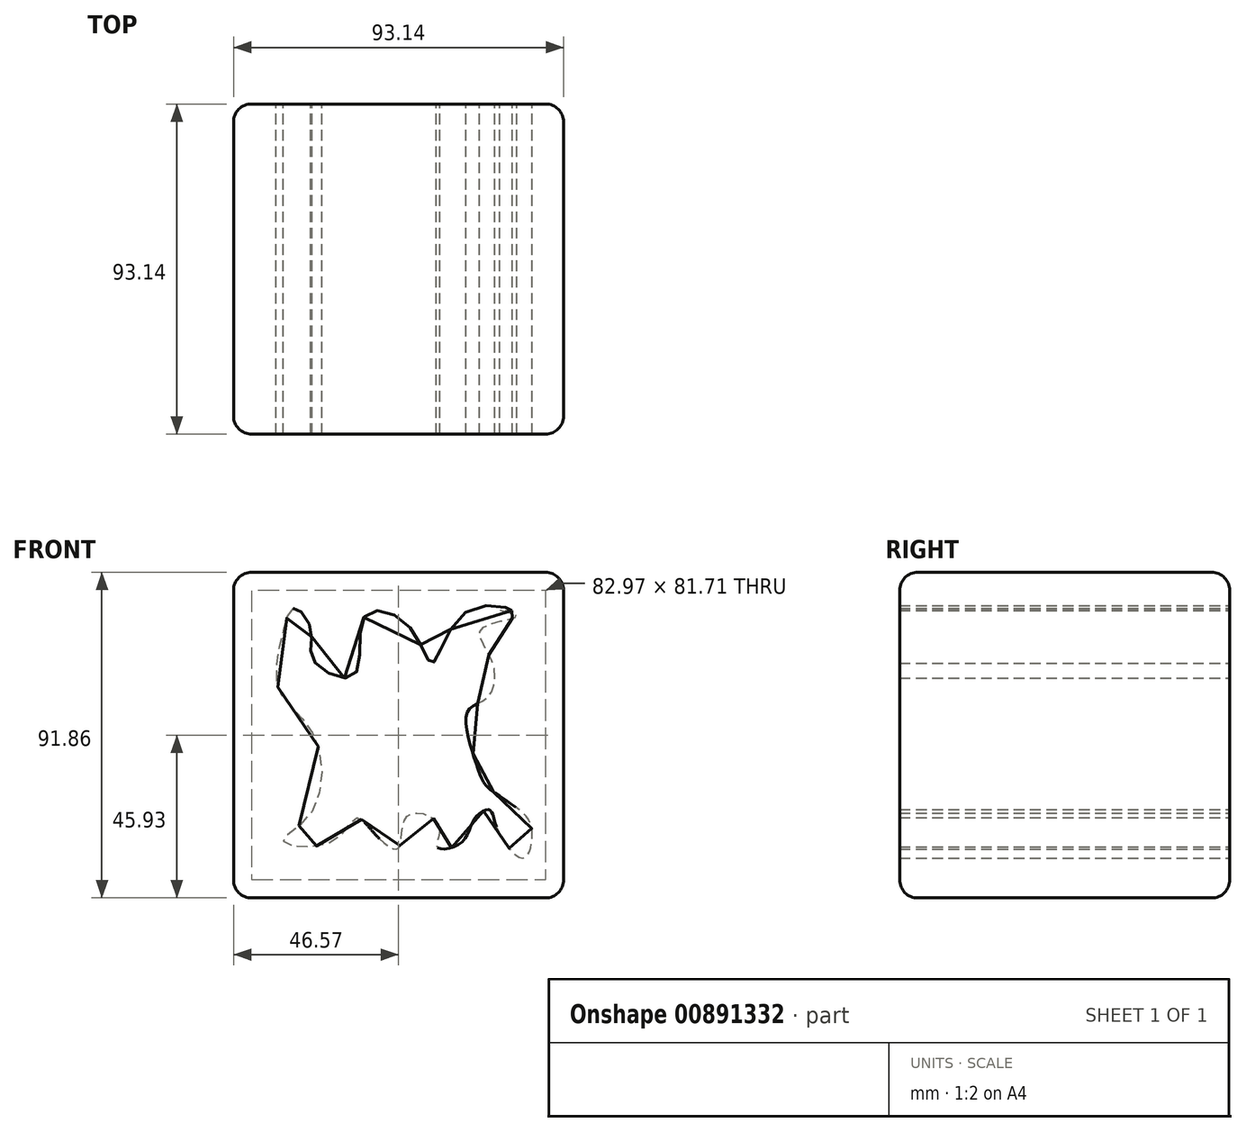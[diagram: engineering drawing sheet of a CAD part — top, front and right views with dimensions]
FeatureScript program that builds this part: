
annotation { "Feature Type Name" : "Feature", "Feature Type Description" : "" }
export const myFeature = defineFeature(function(context is Context, id is Id, definition is map)
    precondition{}
    {
        {
            var Q0;
            Q0=qCreatedBy(makeId("Front.planeOp"),FACE);
            var sketch = newSketch(context, id + "F0", { "sketchPlane" : qUnion([Q0])});
            skLineSegment(sketch, "E0.bottom", {"start": v(46.57, 45.93) * mm, "end": v(-46.57, 45.93) * mm});
            skLineSegment(sketch, "E0.top", {"start": v(46.57, -45.93) * mm, "end": v(-46.57, -45.93) * mm});
            skLineSegment(sketch, "E0.left", {"start": v(46.57, 45.93) * mm, "end": v(46.57, -45.93) * mm});
            skLineSegment(sketch, "E0.right", {"start": v(-46.57, 45.93) * mm, "end": v(-46.57, -45.93) * mm});
            skPoint(sketch, "E0.middle", {"position": v(0, 0) * mm});
            skSolve(sketch);
        }
        {
            var Q0;
            Q0=makeQuery(id+"F0.imprint","IMPRINT",FACE,{"disambiguationData":[TD([[makeQuery(id+"F0.imprint","IMPRINT",EDGE,{"derivedFrom":sQuery(id+"F0.wireOp",EDGE,"E0.bottom")}),1.0]])]});
            extrude(context, id + "F1", {"entities" : qUnion([Q0]), "depth" : 93.14 * mm, "offsetDistance" : 25.4 * mm});
        }
        {
            var Q0;
            Q0=makeQuery(id+"F1.opExtrude","CAP_EDGE",EDGE,{"disambiguationData":[OSD([sQuery(id+"F0.wireOp",EDGE,"E0.bottom")])],"isStart":false});
            var Q1;
            Q1=makeQuery(id+"F1.opExtrude","CAP_EDGE",EDGE,{"disambiguationData":[OSD([sQuery(id+"F0.wireOp",EDGE,"E0.right")])],"isStart":false});
            var Q2;
            Q2=makeQuery(id+"F1.opExtrude","CAP_EDGE",EDGE,{"disambiguationData":[OSD([sQuery(id+"F0.wireOp",EDGE,"E0.top")])],"isStart":false});
            var Q3;
            Q3=makeQuery(id+"F1.opExtrude","CAP_EDGE",EDGE,{"disambiguationData":[OSD([sQuery(id+"F0.wireOp",EDGE,"E0.left")])],"isStart":false});
            var Q4;
            Q4=makeQuery(id+"F1.opExtrude","CAP_EDGE",EDGE,{"disambiguationData":[OSD([sQuery(id+"F0.wireOp",EDGE,"E0.right")])],"isStart":true});
            var Q5;
            Q5=makeQuery(id+"F1.opExtrude","CAP_EDGE",EDGE,{"disambiguationData":[OSD([sQuery(id+"F0.wireOp",EDGE,"E0.bottom")])],"isStart":true});
            var Q6;
            Q6=makeQuery(id+"F1.opExtrude","CAP_FACE",FACE,{"disambiguationData":[OSD([sQuery(id+"F0.wireOp",EDGE,"E0.bottom"),sQuery(id+"F0.wireOp",EDGE,"E0.top"),sQuery(id+"F0.wireOp",EDGE,"E0.left"),sQuery(id+"F0.wireOp",EDGE,"E0.right")])],"isStart":true});
            var Q7;
            Q7=makeQuery(id+"F1.opExtrude","CAP_EDGE",EDGE,{"disambiguationData":[OSD([sQuery(id+"F0.wireOp",EDGE,"E0.top")])],"isStart":true});
            var Q8;
            Q8=makeQuery(id+"F1.opExtrude","CAP_EDGE",EDGE,{"disambiguationData":[OSD([sQuery(id+"F0.wireOp",EDGE,"E0.left")])],"isStart":true});
            var Q9;
            Q9=makeQuery(id+"F1.opExtrude","SWEPT_EDGE",EDGE,{"disambiguationData":[OSD([sQuery(id+"F0.wireOp",EDGE,"E0.bottom"),sQuery(id+"F0.wireOp",EDGE,"E0.left")])]});
            var Q10;
            Q10=makeQuery(id+"F1.opExtrude","SWEPT_EDGE",EDGE,{"disambiguationData":[OSD([sQuery(id+"F0.wireOp",EDGE,"E0.bottom"),sQuery(id+"F0.wireOp",EDGE,"E0.right")])]});
            var Q11;
            Q11=makeQuery(id+"F1.opExtrude","SWEPT_FACE",FACE,{"disambiguationData":[OSD([sQuery(id+"F0.wireOp",EDGE,"E0.left")])]});
            var Q12;
            Q12=makeQuery(id+"F1.opExtrude","SWEPT_EDGE",EDGE,{"disambiguationData":[OSD([sQuery(id+"F0.wireOp",EDGE,"E0.top"),sQuery(id+"F0.wireOp",EDGE,"E0.left")])]});
            var Q13;
            Q13=makeQuery(id+"F1.opExtrude","SWEPT_EDGE",EDGE,{"disambiguationData":[OSD([sQuery(id+"F0.wireOp",EDGE,"E0.top"),sQuery(id+"F0.wireOp",EDGE,"E0.right")])]});
            fillet(context, id + "F2", {"entities" : qUnion([Q0, Q1, Q2, Q3, Q4, Q5, Q6, Q7, Q8, Q9, Q10, Q11, Q12, Q13]), "radius" : 5.08 * mm, "tangentPropagation" : true, "allowEdgeOverflow" : false});
        }
        {
            var Q0;
            Q0=makeQuery(id+"F1.opExtrude","CAP_FACE",FACE,{"disambiguationData":[OSD([sQuery(id+"F0.wireOp",EDGE,"E0.bottom"),sQuery(id+"F0.wireOp",EDGE,"E0.top"),sQuery(id+"F0.wireOp",EDGE,"E0.left"),sQuery(id+"F0.wireOp",EDGE,"E0.right")])],"isStart":false});
            var sketch = newSketch(context, id + "F3", { "sketchPlane" : qUnion([Q0])});
            skFitSpline(sketch, "E1", {"points": [v(32.02, 35.18) * mm, v(19.69, 35.18) * mm, v(9.57, 20.32) * mm, v(2.6, 31.07) * mm, v(-9.72, 33.28) * mm, v(-12.57, 16.84) * mm, v(-23.96, 20.95) * mm, v(-24.59, 29.17) * mm, v(-29.33, 35.81) * mm, v(-32.81, 28.54) * mm, v(-33.76, 12.73) * mm, v(-23.96, 0) * mm, v(-25.22, -22.7) * mm, v(-32.5, -29.96) * mm, v(-18.58, -29.96) * mm, v(-11.94, -23.32) * mm, v(-6.25, -28.38) * mm, v(0, -31.86) * mm, v(2.6, -22.7) * mm, v(11.46, -25.54) * mm, v(10.83, -31.55) * mm, v(17.79, -30.28) * mm, v(21.58, -23.32) * mm, v(25.7, -21.1) * mm, v(27.6, -25.85) * mm, v(35.18, -34.7) * mm, v(37.71, -28.07) * mm, v(35.18, -22.06) * mm, v(26.33, -15.73) * mm, v(23.8, -12.89) * mm, v(20.63, -4.03) * mm, v(19.69, 7.04) * mm, v(25.06, 10.52) * mm, v(26.33, 20.95) * mm, v(23.48, 30.12) * mm, v(33.28, 33.6) * mm, v(28.54, 35.18) * mm, v(32.02, 35.18) * mm]});
            skSolve(sketch);
        }
        {
            var Q0;
            Q0=makeQuery(id+"F3.imprint","IMPRINT",FACE,{"disambiguationData":[TD([[makeQuery(id+"F3.imprint","IMPRINT",EDGE,{"derivedFrom":sQuery(id+"F3.wireOp",EDGE,"E1")}),1.0]])]});
            extrude(context, id + "F4", {"entities" : qUnion([Q0]), "operationType" : NewBodyOperationType.REMOVE, "oppositeDirection" : true, "depth" : 101.6 * mm, "offsetDistance" : 25.4 * mm});
        }
    });
